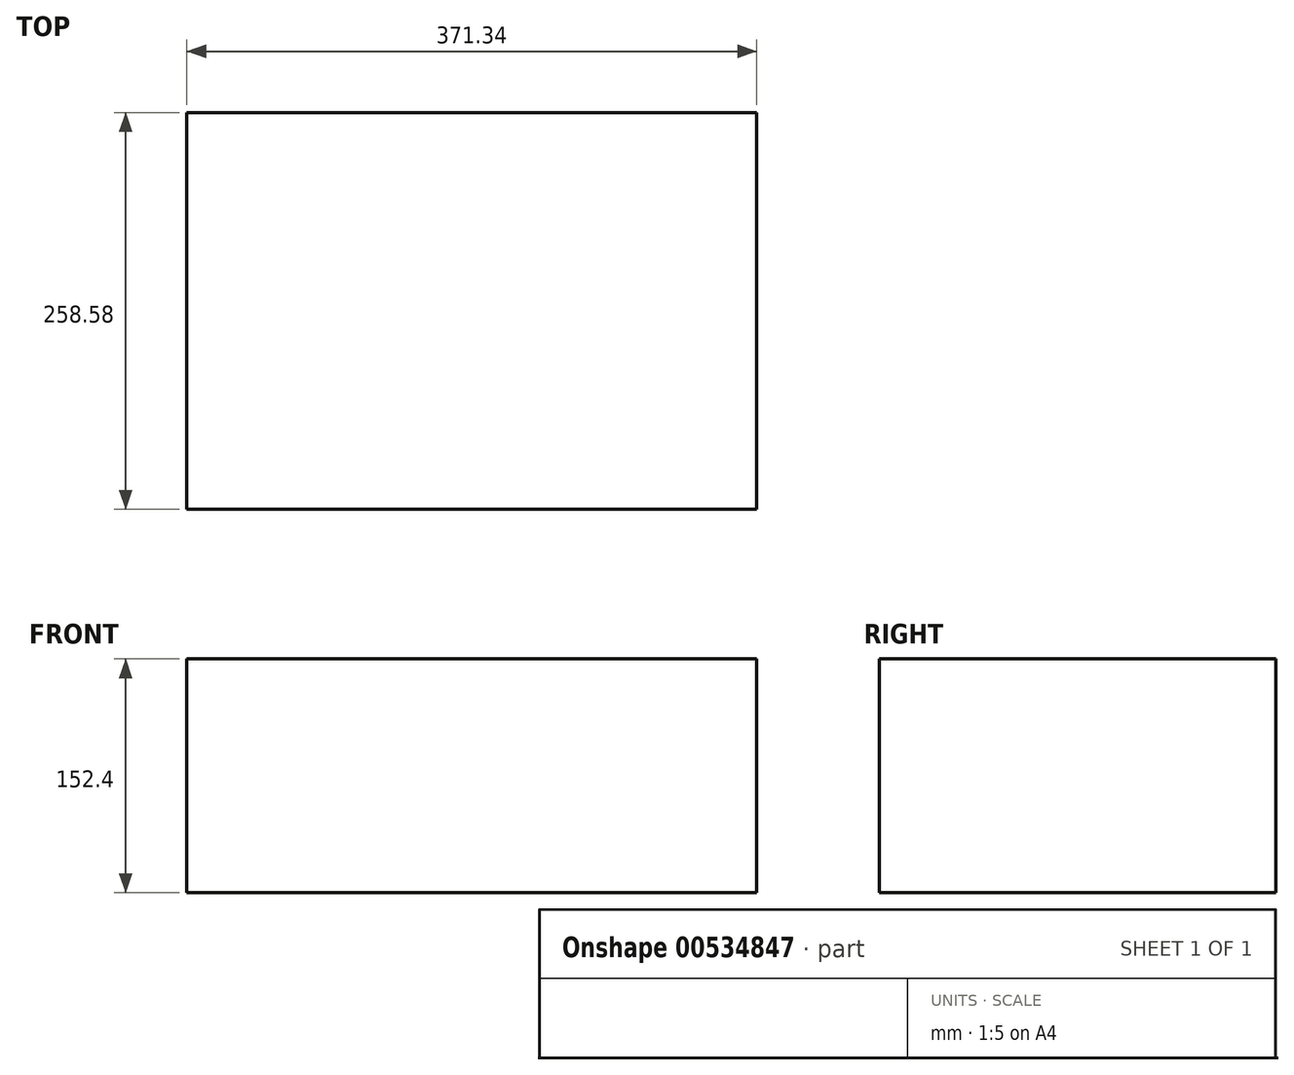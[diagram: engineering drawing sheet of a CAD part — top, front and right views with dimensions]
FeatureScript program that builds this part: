
annotation { "Feature Type Name" : "Feature", "Feature Type Description" : "" }
export const myFeature = defineFeature(function(context is Context, id is Id, definition is map)
    precondition{}
    {
        {
            var Q0;
            Q0=qCreatedBy(makeId("Top.planeOp"),FACE);
            var sketch = newSketch(context, id + "F0", { "sketchPlane" : qUnion([Q0])});
            skLineSegment(sketch, "E0.bottom", {"start": v(185.67, -129.29) * mm, "end": v(-185.67, -129.29) * mm});
            skLineSegment(sketch, "E0.top", {"start": v(185.67, 129.29) * mm, "end": v(-185.67, 129.29) * mm});
            skLineSegment(sketch, "E0.left", {"start": v(185.67, -129.29) * mm, "end": v(185.67, 129.29) * mm});
            skLineSegment(sketch, "E0.right", {"start": v(-185.67, -129.29) * mm, "end": v(-185.67, 129.29) * mm});
            skPoint(sketch, "E0.middle", {"position": v(0, 0) * mm});
            skSolve(sketch);
        }
        {
            var Q0;
            Q0=makeQuery(id+"F0.imprint","IMPRINT",FACE,{"disambiguationData":[TD([[makeQuery(id+"F0.imprint","IMPRINT",EDGE,{"derivedFrom":sQuery(id+"F0.wireOp",EDGE,"E0.bottom")}),-1.0]])]});
            extrude(context, id + "F1", {"entities" : qUnion([Q0]), "depth" : 152.4 * mm, "offsetDistance" : 25 * mm});
        }
    });
